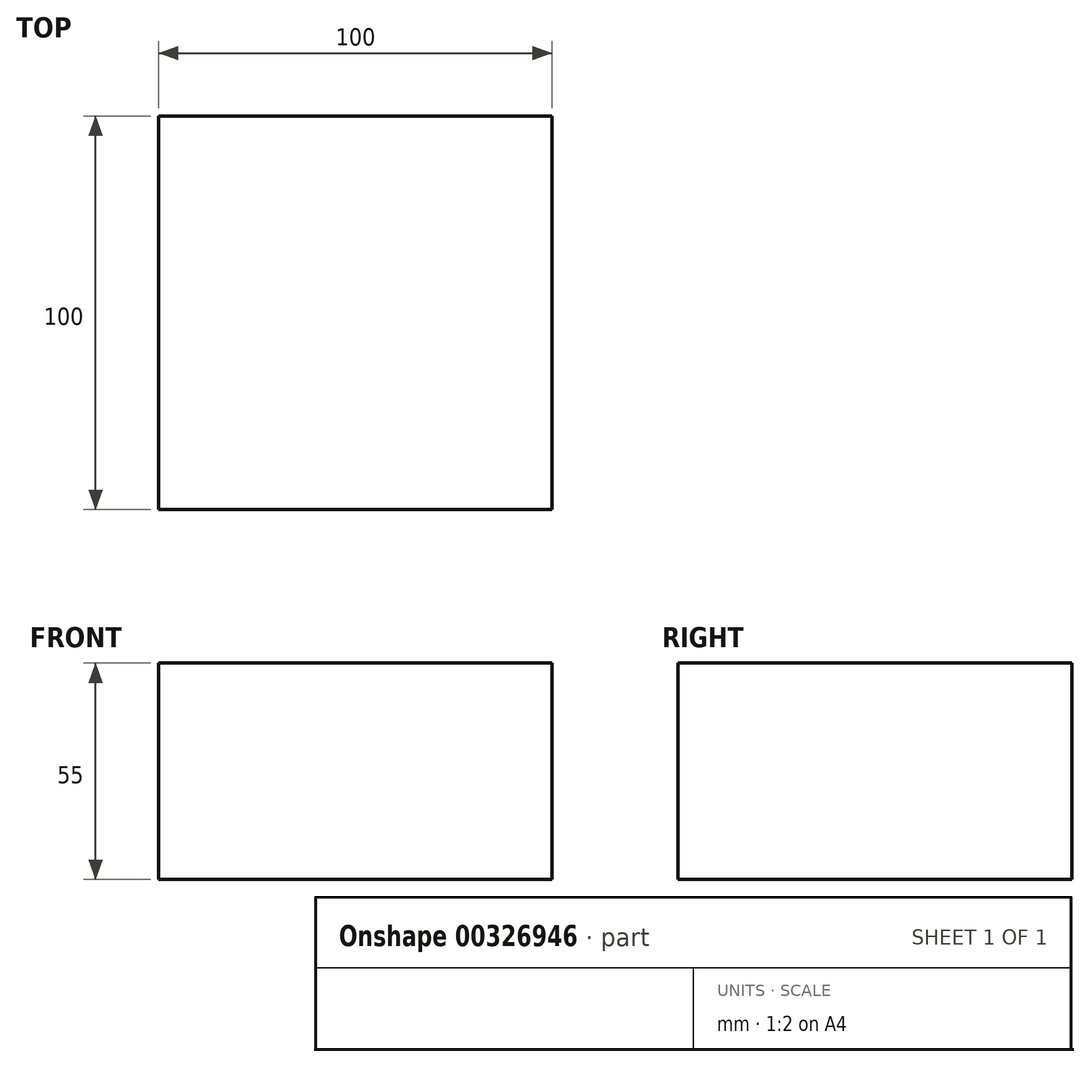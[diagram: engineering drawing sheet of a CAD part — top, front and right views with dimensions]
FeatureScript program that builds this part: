
annotation { "Feature Type Name" : "Feature", "Feature Type Description" : "" }
export const myFeature = defineFeature(function(context is Context, id is Id, definition is map)
    precondition{}
    {
        {
            var Q0;
            Q0=qCreatedBy(makeId("Top.planeOp"),FACE);
            var sketch = newSketch(context, id + "F0", { "sketchPlane" : qUnion([Q0])});
            skLineSegment(sketch, "E0.bottom", {"start": v(-50.9, -44.07) * mm, "end": v(49.1, -44.07) * mm});
            skLineSegment(sketch, "E0.top", {"start": v(-50.9, 55.93) * mm, "end": v(49.1, 55.93) * mm});
            skLineSegment(sketch, "E0.left", {"start": v(-50.9, -44.07) * mm, "end": v(-50.9, 55.93) * mm});
            skLineSegment(sketch, "E0.right", {"start": v(49.1, -44.07) * mm, "end": v(49.1, 55.93) * mm});
            skSolve(sketch);
        }
        {
            var Q0;
            Q0 = qSketchRegion(id + "F0", true);
            extrude(context, id + "F1", {"entities" : qUnion([Q0]), "depth" : 55 * mm});
        }
    });
